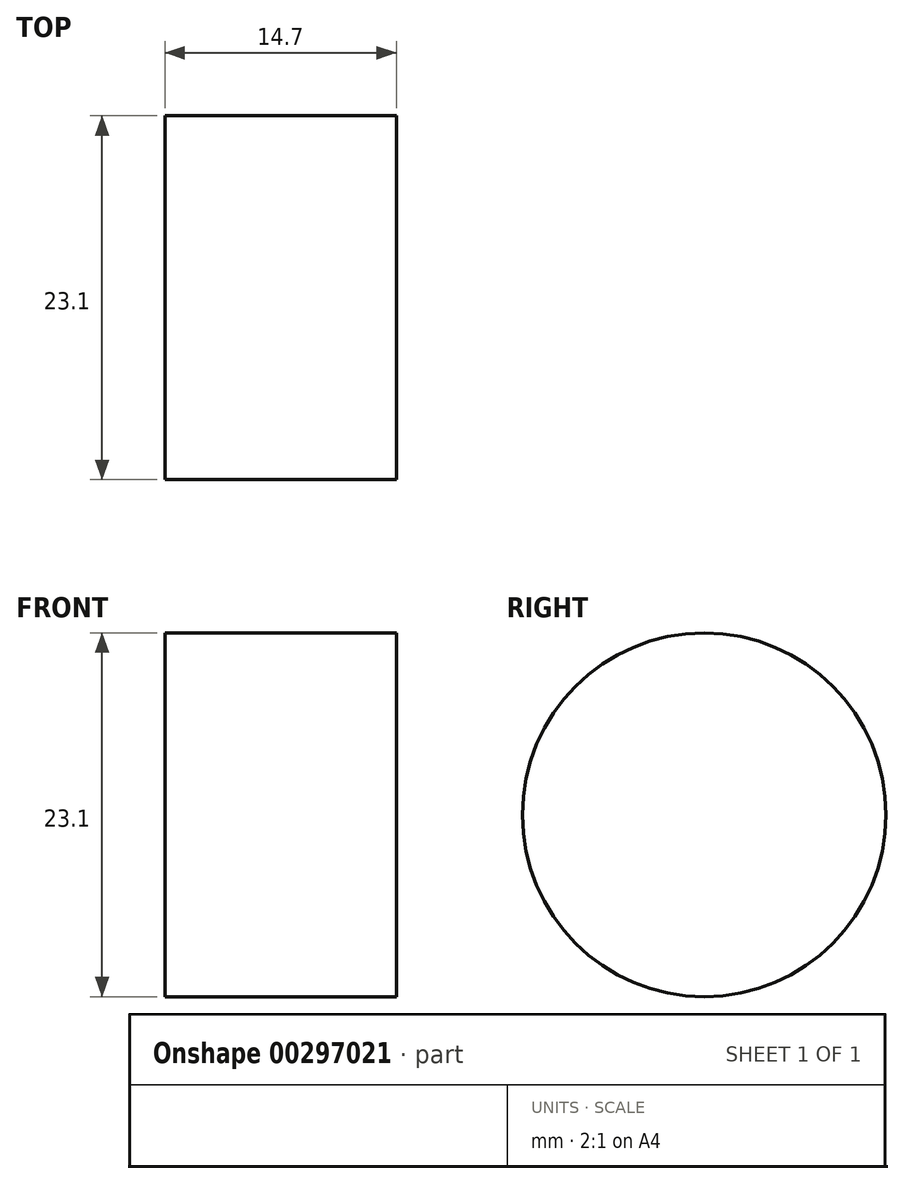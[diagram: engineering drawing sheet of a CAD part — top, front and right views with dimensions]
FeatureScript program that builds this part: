
annotation { "Feature Type Name" : "Feature", "Feature Type Description" : "" }
export const myFeature = defineFeature(function(context is Context, id is Id, definition is map)
    precondition{}
    {
        {
            var Q0;
            Q0=qCreatedBy(makeId("Front.planeOp"),FACE);
            var sketch = newSketch(context, id + "F0", { "sketchPlane" : qUnion([Q0])});
            skLineSegment(sketch, "E0.bottom", {"start": v(-14.7, 11.55) * mm, "end": v(0, 11.55) * mm});
            skLineSegment(sketch, "E0.top", {"start": v(-14.7, -11.55) * mm, "end": v(0, -11.55) * mm});
            skLineSegment(sketch, "E0.left", {"start": v(-14.7, 11.55) * mm, "end": v(-14.7, -11.55) * mm});
            skLineSegment(sketch, "E0.right", {"start": v(0, 11.55) * mm, "end": v(0, -11.55) * mm});
            skLineSegment(sketch, "E1.bottom", {"start": v(-14.7, -7.65) * mm, "end": v(-14.7, -7.65) * mm});
            skLineSegment(sketch, "E1.top", {"start": v(-14.7, 7.65) * mm, "end": v(-14.7, 7.65) * mm});
            skLineSegment(sketch, "E1.left", {"start": v(-14.7, 7.65) * mm, "end": v(-14.7, -7.65) * mm});
            skLineSegment(sketch, "E1.right", {"start": v(-14.7, 7.65) * mm, "end": v(-14.7, -7.65) * mm});
            skLineSegment(sketch, "E2", {"start": v(0, 0) * mm, "end": v(-14.7, 0) * mm});
            skSolve(sketch);
        }
        {
            var Q0;
            {var subQ5=sQuery(id+"F0.wireOp",EDGE,"E0.bottom");Q0=makeQuery(id+"F0.imprint","IMPRINT",FACE,{"disambiguationData":[TD([[makeQuery(id+"F0.imprint","IMPRINT",EDGE,{"derivedFrom":subQ5}),-1.0]])]});}
            var Q1;
            Q1=sQuery(id+"F0.wireOp",EDGE,"E2");
            revolve(context, id + "F1", {"entities" : qUnion([Q0]), "axis" : qUnion([Q1]), "revolveType" : RevolveType.FULL});
        }
    });
